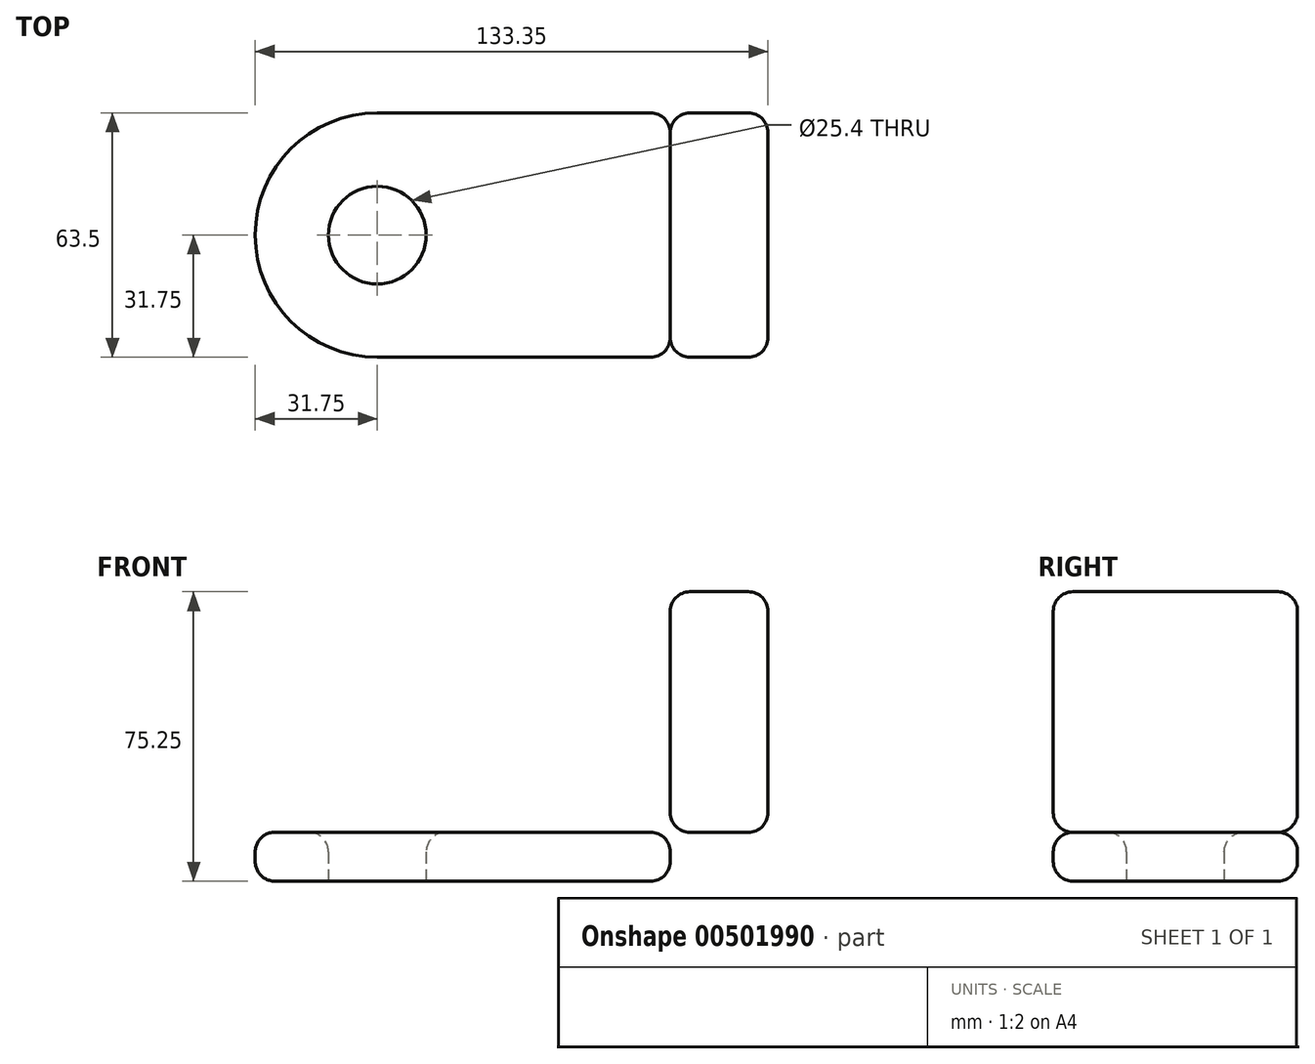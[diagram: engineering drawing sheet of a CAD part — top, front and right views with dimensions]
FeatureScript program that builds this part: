
annotation { "Feature Type Name" : "Feature", "Feature Type Description" : "" }
export const myFeature = defineFeature(function(context is Context, id is Id, definition is map)
    precondition{}
    {
        {
            var Q0;
            Q0=qCreatedBy(makeId("Top.planeOp"),FACE);
            var sketch = newSketch(context, id + "F0", { "sketchPlane" : qUnion([Q0])});
            skLineSegment(sketch, "E0.bottom", {"start": v(-38.1, 31.75) * mm, "end": v(38.1, 31.75) * mm});
            skLineSegment(sketch, "E0.top", {"start": v(-38.1, -31.75) * mm, "end": v(38.1, -31.75) * mm});
            skLineSegment(sketch, "E0.left", {"start": v(-38.1, 31.75) * mm, "end": v(-38.1, -31.75) * mm});
            skLineSegment(sketch, "E0.right", {"start": v(38.1, 31.75) * mm, "end": v(38.1, -31.75) * mm});
            skPoint(sketch, "E0.middle", {"position": v(0, 0) * mm});
            skCircle(sketch, "E1", {"center": v(-38.1, 0) * mm, "radius": 31.75 * mm});
            skCircle(sketch, "E2", {"center": v(-38.1, 0) * mm, "radius": 12.7 * mm});
            skSolve(sketch);
        }
        {
            var Q0;
            {var subQ1=sQuery(id+"F0.wireOp",EDGE,"E0.left");var subQ3=sQuery(id+"F0.wireOp",EDGE,"E2");var subQ4=makeQuery(id+"F0.imprint","INTERSECT",VERTEX,{"disambiguationData":[OD(0.0)],"derivedFrom":[subQ1,subQ3]});Q0=makeQuery(id+"F0.imprint","IMPRINT",FACE,{"disambiguationData":[TD([[makeQuery(id+"F0.imprint","IMPRINT",EDGE,{"disambiguationData":[TD([[subQ4,-1.0]])],"derivedFrom":subQ3}),-1.0]])]});}
            var Q1;
            {var subQ1=sQuery(id+"F0.wireOp",EDGE,"E0.left");var subQ3=sQuery(id+"F0.wireOp",EDGE,"E2");var subQ4=makeQuery(id+"F0.imprint","INTERSECT",VERTEX,{"disambiguationData":[OD(0.0)],"derivedFrom":[subQ1,subQ3]});Q1=makeQuery(id+"F0.imprint","IMPRINT",FACE,{"disambiguationData":[TD([[makeQuery(id+"F0.imprint","IMPRINT",EDGE,{"disambiguationData":[TD([[subQ4,1.0]])],"derivedFrom":subQ3}),-1.0]])]});}
            var Q2;
            {var subQ0=sQuery(id+"F0.wireOp",EDGE,"E0.bottom");Q2=makeQuery(id+"F0.imprint","IMPRINT",FACE,{"disambiguationData":[TD([[makeQuery(id+"F0.imprint","IMPRINT",EDGE,{"derivedFrom":subQ0}),-1.0]])]});}
            extrude(context, id + "F1", {"entities" : qUnion([Q0, Q1, Q2]), "depth" : 12.7 * mm});
        }
        {
            var Q0;
            Q0=makeQuery(id+"F1.opExtrude","SWEPT_FACE",FACE,{"disambiguationData":[OSD([sQuery(id+"F0.wireOp",EDGE,"E0.right")])]});
            var sketch = newSketch(context, id + "F2", { "sketchPlane" : qUnion([Q0])});
            skLineSegment(sketch, "E3.bottom", {"start": v(31.75, 0) * mm, "end": v(-31.75, 0) * mm});
            skLineSegment(sketch, "E3.top", {"start": v(31.75, 75.25) * mm, "end": v(-31.75, 75.25) * mm});
            skLineSegment(sketch, "E3.left", {"start": v(31.75, 0) * mm, "end": v(31.75, 75.25) * mm});
            skLineSegment(sketch, "E3.right", {"start": v(-31.75, 0) * mm, "end": v(-31.75, 75.25) * mm});
            skLineSegment(sketch, "E4.top", {"start": v(36.78, 12.7) * mm, "end": v(-29.47, 12.7) * mm});
            skSolve(sketch);
        }
        {
            var Q0;
            {var subQ3=sQuery(id+"F2.wireOp",EDGE,"E3.top");Q0=makeQuery(id+"F2.imprint","IMPRINT",FACE,{"disambiguationData":[TD([[makeQuery(id+"F2.imprint","IMPRINT",EDGE,{"derivedFrom":subQ3}),1.0]])]});}
            extrude(context, id + "F3", {"entities" : qUnion([Q0]), "depth" : 25.4 * mm});
        }
        {
            var Q0;
            Q0=makeQuery(id+"F1.opExtrude","CAP_EDGE",EDGE,{"disambiguationData":[OSD([sQuery(id+"F0.wireOp",EDGE,"E0.right")])],"isStart":true});
            var Q1;
            Q1=makeQuery(id+"F3.opExtrude","CAP_EDGE",EDGE,{"disambiguationData":[OSD([sQuery(id+"F0.wireOp",EDGE,"E0.right"),sQuery(id+"F2.wireOp",EDGE,"E4.top")])],"isStart":false});
            var Q2;
            Q2=makeQuery(id+"F1.opExtrude","CAP_EDGE",EDGE,{"disambiguationData":[OSD([sQuery(id+"F0.wireOp",EDGE,"E0.right")])],"isStart":false});
            fillet(context, id + "F4", {"entities" : qUnion([Q0, Q1, Q2]), "radius" : 5.08 * mm, "tangentPropagation" : true, "allowEdgeOverflow" : false});
        }
        {
            var Q0;
            Q0=makeQuery(id+"F3.opExtrude","CAP_EDGE",EDGE,{"disambiguationData":[OSD([sQuery(id+"F0.wireOp",EDGE,"E0.right"),sQuery(id+"F2.wireOp",EDGE,"E4.top")])],"isStart":true});
            fillet(context, id + "F5", {"entities" : qUnion([Q0]), "radius" : 5.08 * mm, "tangentPropagation" : true, "allowEdgeOverflow" : false});
        }
        {
            var Q0;
            Q0=makeQuery(id+"F3.opExtrude","CAP_EDGE",EDGE,{"disambiguationData":[OSD([sQuery(id+"F2.wireOp",EDGE,"E3.top")])],"isStart":false});
            fillet(context, id + "F6", {"entities" : qUnion([Q0]), "radius" : 5.08 * mm, "tangentPropagation" : true, "allowEdgeOverflow" : false});
        }
        {
            var Q0;
            Q0=makeQuery(id+"F3.opExtrude","SWEPT_FACE",FACE,{"disambiguationData":[OSD([sQuery(id+"F2.wireOp",EDGE,"E3.top")])]});
            fillet(context, id + "F7", {"entities" : qUnion([Q0]), "radius" : 5.08 * mm, "tangentPropagation" : true, "allowEdgeOverflow" : false});
        }
        {
            var Q0;
            Q0=makeQuery(id+"F1.opExtrude","CAP_EDGE",EDGE,{"disambiguationData":[OSD([sQuery(id+"F0.wireOp",EDGE,"E1")])],"isStart":true});
            fillet(context, id + "F8", {"entities" : qUnion([Q0]), "radius" : 5.08 * mm, "tangentPropagation" : true, "allowEdgeOverflow" : false});
        }
        {
            var Q0;
            Q0=makeQuery(id+"F1.opExtrude","CAP_EDGE",EDGE,{"disambiguationData":[OSD([sQuery(id+"F0.wireOp",EDGE,"E2")])],"isStart":false});
            var Q1;
            {var subQ0=sQuery(id+"F0.wireOp",EDGE,"E1");Q1=makeQuery(id+"F8.opFillet","BLEND_EDGE",EDGE,{"blendedFrom":[makeQuery(id+"F1.opExtrude","CAP_EDGE",EDGE,{"disambiguationData":[OSD([subQ0])],"isStart":false}),makeQuery(id+"F1.opExtrude","CAP_FACE",FACE,{"disambiguationData":[OSD([sQuery(id+"F0.wireOp",EDGE,"E0.bottom"),sQuery(id+"F0.wireOp",EDGE,"E0.top"),sQuery(id+"F0.wireOp",EDGE,"E0.right"),subQ0,sQuery(id+"F0.wireOp",EDGE,"E2")])],"isStart":false})],"blendedInto":[makeQuery(id+"F1.opExtrude","CAP_FACE",FACE,{"disambiguationData":[OSD([sQuery(id+"F0.wireOp",EDGE,"E0.bottom"),sQuery(id+"F0.wireOp",EDGE,"E0.top"),sQuery(id+"F0.wireOp",EDGE,"E0.right"),subQ0,sQuery(id+"F0.wireOp",EDGE,"E2")])],"isStart":false})]});}
            var Q2;
            {var subQ0=sQuery(id+"F0.wireOp",EDGE,"E0.bottom");Q2=makeQuery(id+"F8.opFillet","BLEND_EDGE",EDGE,{"blendedFrom":[makeQuery(id+"F1.opExtrude","CAP_EDGE",EDGE,{"disambiguationData":[OSD([subQ0])],"isStart":false}),makeQuery(id+"F1.opExtrude","CAP_FACE",FACE,{"disambiguationData":[OSD([subQ0,sQuery(id+"F0.wireOp",EDGE,"E0.top"),sQuery(id+"F0.wireOp",EDGE,"E0.right"),sQuery(id+"F0.wireOp",EDGE,"E1"),sQuery(id+"F0.wireOp",EDGE,"E2")])],"isStart":false})],"blendedInto":[makeQuery(id+"F1.opExtrude","CAP_FACE",FACE,{"disambiguationData":[OSD([subQ0,sQuery(id+"F0.wireOp",EDGE,"E0.top"),sQuery(id+"F0.wireOp",EDGE,"E0.right"),sQuery(id+"F0.wireOp",EDGE,"E1"),sQuery(id+"F0.wireOp",EDGE,"E2")])],"isStart":false})]});}
            var Q3;
            {var subQ0=sQuery(id+"F0.wireOp",EDGE,"E0.top");Q3=makeQuery(id+"F8.opFillet","BLEND_EDGE",EDGE,{"blendedFrom":[makeQuery(id+"F1.opExtrude","CAP_EDGE",EDGE,{"disambiguationData":[OSD([subQ0])],"isStart":false}),makeQuery(id+"F1.opExtrude","CAP_FACE",FACE,{"disambiguationData":[OSD([sQuery(id+"F0.wireOp",EDGE,"E0.bottom"),subQ0,sQuery(id+"F0.wireOp",EDGE,"E0.right"),sQuery(id+"F0.wireOp",EDGE,"E1"),sQuery(id+"F0.wireOp",EDGE,"E2")])],"isStart":false})],"blendedInto":[makeQuery(id+"F1.opExtrude","CAP_FACE",FACE,{"disambiguationData":[OSD([sQuery(id+"F0.wireOp",EDGE,"E0.bottom"),subQ0,sQuery(id+"F0.wireOp",EDGE,"E0.right"),sQuery(id+"F0.wireOp",EDGE,"E1"),sQuery(id+"F0.wireOp",EDGE,"E2")])],"isStart":false})]});}
            var Q4;
            {var subQ0=sQuery(id+"F0.wireOp",EDGE,"E0.top");Q4=makeQuery(id+"F8.opFillet","BLEND_EDGE",EDGE,{"blendedFrom":[makeQuery(id+"F1.opExtrude","CAP_EDGE",EDGE,{"disambiguationData":[OSD([subQ0])],"isStart":false}),makeQuery(id+"F1.opExtrude","SWEPT_FACE",FACE,{"disambiguationData":[OSD([subQ0])]})],"blendedInto":[makeQuery(id+"F1.opExtrude","SWEPT_FACE",FACE,{"disambiguationData":[OSD([subQ0])]})]});}
            var Q5;
            Q5=makeQuery(id+"F8.opFillet","BLEND_EDGE",EDGE,{"blendedFrom":[makeQuery(id+"F1.opExtrude","CAP_EDGE",EDGE,{"disambiguationData":[OSD([sQuery(id+"F0.wireOp",EDGE,"E1")])],"isStart":false}),makeQuery(id+"F1.opExtrude","CAP_EDGE",EDGE,{"disambiguationData":[OSD([sQuery(id+"F0.wireOp",EDGE,"E0.top")])],"isStart":false})],"blendedInto":[]});
            var Q6;
            Q6=makeQuery(id+"F8.opFillet","BLEND_EDGE",EDGE,{"blendedFrom":[makeQuery(id+"F1.opExtrude","CAP_EDGE",EDGE,{"disambiguationData":[OSD([sQuery(id+"F0.wireOp",EDGE,"E1")])],"isStart":false}),makeQuery(id+"F1.opExtrude","CAP_EDGE",EDGE,{"disambiguationData":[OSD([sQuery(id+"F0.wireOp",EDGE,"E0.bottom")])],"isStart":false})],"blendedInto":[]});
            fillet(context, id + "F9", {"entities" : qUnion([Q0, Q1, Q2, Q3, Q4, Q5, Q6]), "radius" : 5.08 * mm, "tangentPropagation" : true, "allowEdgeOverflow" : false});
        }
    });
